# Revit family: PRESTO ARTE-I 2D con llave
name_source: partatom
category: Aparatos sanitarios
revit_build: Autodesk Revit 2015 (Build: 20140223_1515(x64)
units: mm (PartAtom-declared; Revit-internal decimal feet)

## types (1)
- 15150
    Accionamiento = Por pulsador
    Comentarios de tipo = Suministrado con tuerca y casquillo para tubo de Ø 28 mm
◦ Con dispositivo antiSifónico que asegura la protección de la red de agua potable contra las eventuales absorciones de agua contaminada
◦ Cabeza intercambiable que comprende todo el mecanismo del fluxor
◦ Apertura por pulsador
◦ Cuerpo del fluxor en latón cromado con piezas interiores en materiales resistentes a la corrosión y a las incrustaciones calcáreas
◦ Nível de ruído categoria II según normativa vigente EN-200
◦ Cabeza compatible con fluxor Presto 1000 C y Presto ARTE-I.
    Conexión AC = Sí
    Conexión AF = Sí
    Código de montaje = C1030220
    Descripción = Fluxor temporizado de fijación sobre muro con cuerpo y embellecedor en latón cromado. Dispositivo antiSifónico incorporado. Pistón intercambiable.
    ENTRADA = Macho 3/4"
    Elevación por defecto = 1219 mm
    Fabricante = PRESTO IBÉRICA
    Imagen de tipo = <Ninguno>
    Material = LATON CROMADO
    Modelo = PRESTO XT I 2D CON LLAVE
    PESO BRUTO = 0.790 Kg
    REFERENCIA = 15150
    TIPO DE AGUA = Fria
    Teléfono = (+34) 915 782 575
    URL = http://www.prestoiberica.com

## geometry (parser evidence)
native form markers: Blend x3
no freeform markers — native parametric forms only
